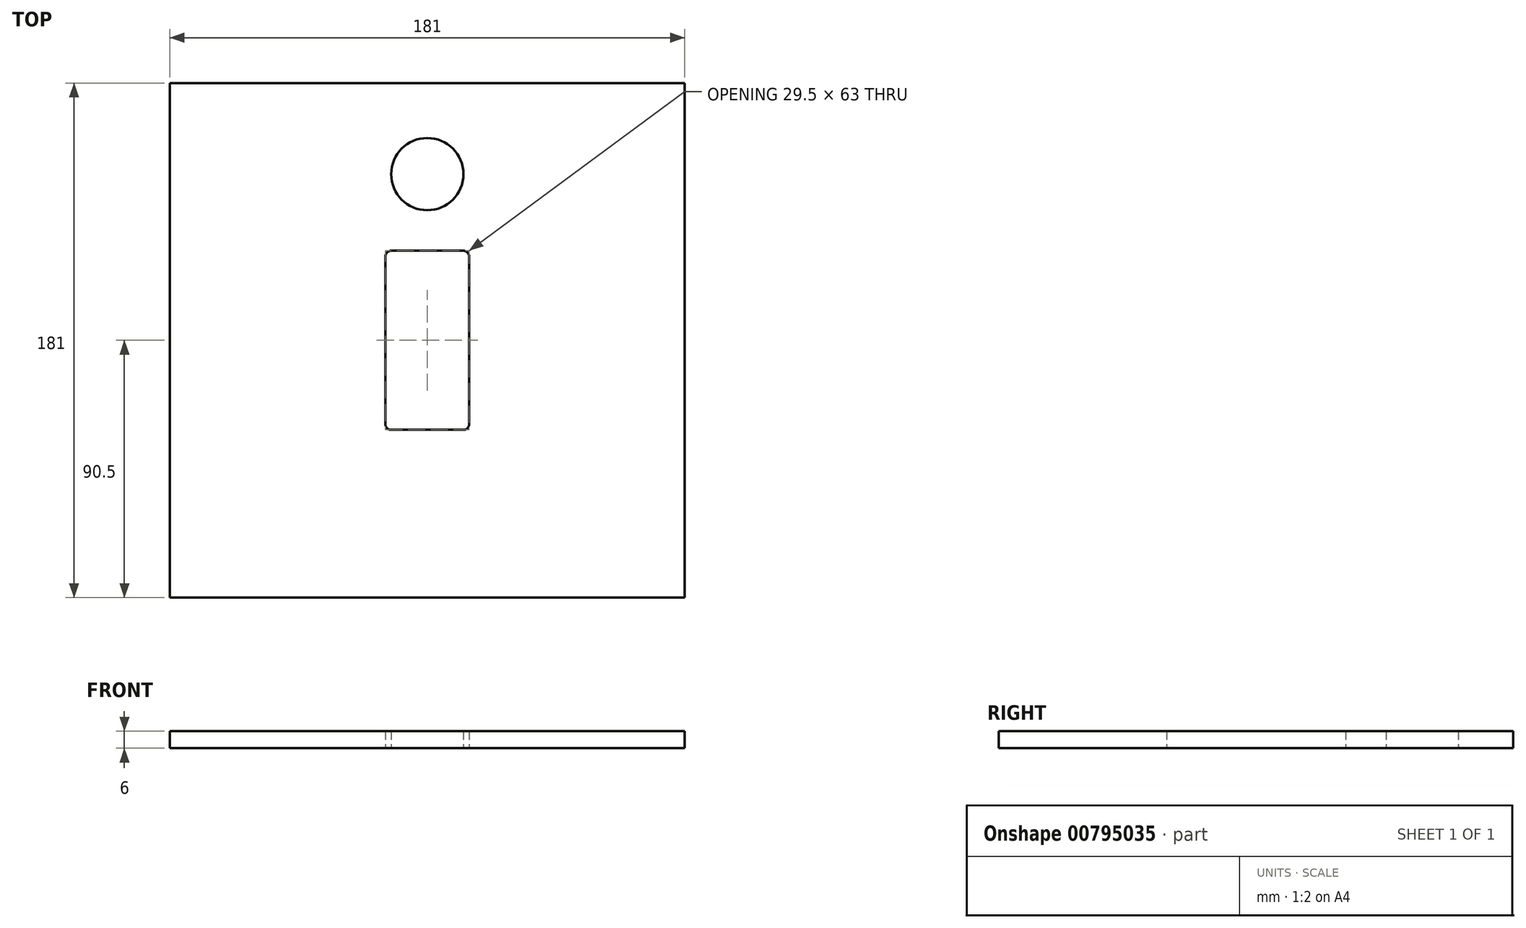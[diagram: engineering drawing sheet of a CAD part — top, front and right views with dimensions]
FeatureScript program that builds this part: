
annotation { "Feature Type Name" : "Feature", "Feature Type Description" : "" }
export const myFeature = defineFeature(function(context is Context, id is Id, definition is map)
    precondition{}
    {
        {
            var Q0;
            Q0=qCreatedBy(makeId("Top.planeOp"),FACE);
            var sketch = newSketch(context, id + "F0", { "sketchPlane" : qUnion([Q0])});
            skLineSegment(sketch, "E0.bottom", {"start": v(90.5, 90.5) * mm, "end": v(-90.5, 90.5) * mm});
            skLineSegment(sketch, "E0.top", {"start": v(90.5, -90.5) * mm, "end": v(-90.5, -90.5) * mm});
            skLineSegment(sketch, "E0.left", {"start": v(90.5, 90.5) * mm, "end": v(90.5, -90.5) * mm});
            skLineSegment(sketch, "E0.right", {"start": v(-90.5, 90.5) * mm, "end": v(-90.5, -90.5) * mm});
            skPoint(sketch, "E0.middle", {"position": v(0, 0) * mm});
            skLineSegment(sketch, "E1.bottom", {"start": v(12.75, 31.5) * mm, "end": v(-12.75, 31.5) * mm});
            skLineSegment(sketch, "E1.top", {"start": v(12.75, -31.5) * mm, "end": v(-12.75, -31.5) * mm});
            skLineSegment(sketch, "E1.left", {"start": v(14.75, 29.5) * mm, "end": v(14.75, -29.5) * mm});
            skLineSegment(sketch, "E1.right", {"start": v(-14.75, 29.5) * mm, "end": v(-14.75, -29.5) * mm});
            skPoint(sketch, "E2.visualSharp", {"position": v(-14.75, 31.5) * mm});
            skArc(sketch, "E2.filletArc", {"start": v(-12.75, 31.5) * mm, "mid": v(-14.16, 30.91) * mm, "end": v(-14.75, 29.5) * mm});
            skPoint(sketch, "E3.visualSharp", {"position": v(14.75, 31.5) * mm});
            skArc(sketch, "E3.filletArc", {"start": v(14.75, 29.5) * mm, "mid": v(14.16, 30.91) * mm, "end": v(12.75, 31.5) * mm});
            skPoint(sketch, "E4.visualSharp", {"position": v(14.75, -31.5) * mm});
            skArc(sketch, "E4.filletArc", {"start": v(12.75, -31.5) * mm, "mid": v(14.16, -30.91) * mm, "end": v(14.75, -29.5) * mm});
            skPoint(sketch, "E5.visualSharp", {"position": v(-14.75, -31.5) * mm});
            skArc(sketch, "E5.filletArc", {"start": v(-14.75, -29.5) * mm, "mid": v(-14.16, -30.91) * mm, "end": v(-12.75, -31.5) * mm});
            skCircle(sketch, "E6", {"center": v(0, 58.48) * mm, "radius": 12.7 * mm});
            skSolve(sketch);
        }
        {
            var Q0;
            Q0=makeQuery(id+"F0.imprint","IMPRINT",FACE,{"disambiguationData":[TD([[makeQuery(id+"F0.imprint","IMPRINT",EDGE,{"derivedFrom":sQuery(id+"F0.wireOp",EDGE,"E0.bottom")}),1.0]])]});
            extrude(context, id + "F1", {"entities" : qUnion([Q0]), "depth" : 6 * mm, "offsetDistance" : 25 * mm});
        }
    });
